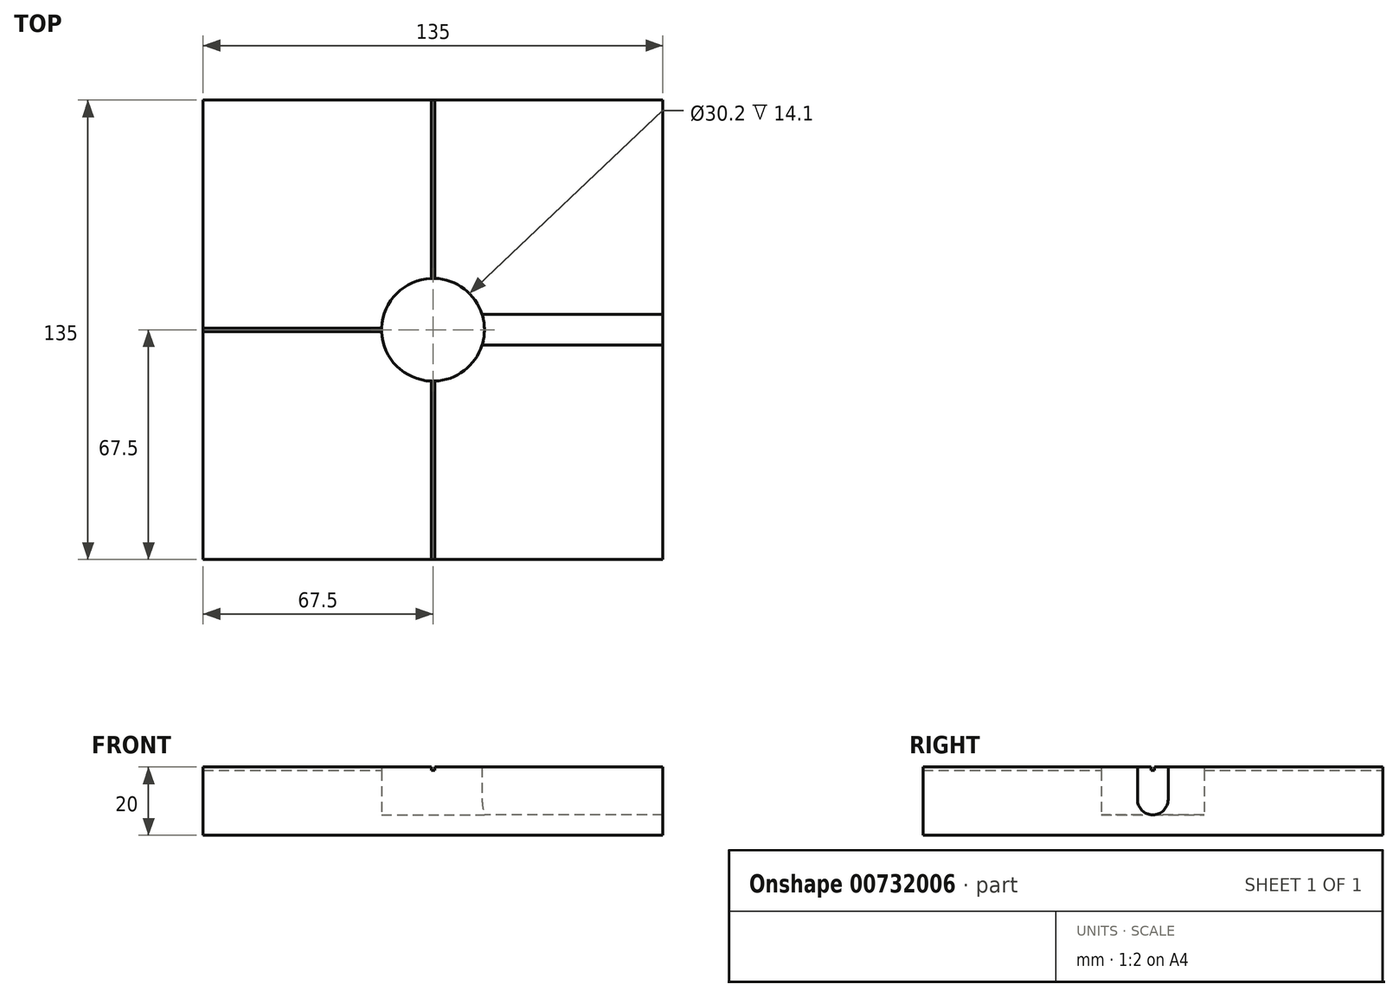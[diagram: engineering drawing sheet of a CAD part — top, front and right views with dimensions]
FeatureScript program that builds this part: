
annotation { "Feature Type Name" : "Feature", "Feature Type Description" : "" }
export const myFeature = defineFeature(function(context is Context, id is Id, definition is map)
    precondition{}
    {
        {
            var Q0;
            Q0=qCreatedBy(makeId("Front.planeOp"),FACE);
            var sketch = newSketch(context, id + "F0", { "sketchPlane" : qUnion([Q0])});
            skLineSegment(sketch, "E0", {"start": v(15.1, 20) * mm, "end": v(15.1, 5.9) * mm});
            skLineSegment(sketch, "E1", {"start": v(15.1, 5.9) * mm, "end": v(0, 5.9) * mm});
            skLineSegment(sketch, "E2", {"start": v(15.1, 20) * mm, "end": v(0, 20) * mm});
            skLineSegment(sketch, "E3", {"start": v(0, 20) * mm, "end": v(0, 5.9) * mm});
            skSolve(sketch);
        }
        {
            var Q0;
            Q0=qCreatedBy(makeId("Right.planeOp"),FACE);
            var sketch = newSketch(context, id + "F1", { "sketchPlane" : qUnion([Q0])});
            skLineSegment(sketch, "E4", {"start": v(0, 20.46) * mm, "end": v(-4.5, 20.46) * mm});
            skLineSegment(sketch, "E5", {"start": v(4.5, 20.46) * mm, "end": v(0, 20.46) * mm});
            skLineSegment(sketch, "E6", {"start": v(4.5, 20.46) * mm, "end": v(4.5, 10.46) * mm});
            skLineSegment(sketch, "E7", {"start": v(-4.5, 20.46) * mm, "end": v(-4.5, 10.46) * mm});
            skArc(sketch, "E8", {"start": v(4.5, 10.46) * mm, "mid": v(0, 5.96) * mm, "end": v(-4.5, 10.46) * mm});
            skSolve(sketch);
        }
        {
            var Q0;
            Q0=qCreatedBy(makeId("Top.planeOp"),FACE);
            var sketch = newSketch(context, id + "F2", { "sketchPlane" : qUnion([Q0])});
            skLineSegment(sketch, "E9", {"start": v(14, 0) * mm, "end": v(14, -0.5) * mm});
            skLineSegment(sketch, "E10", {"start": v(14, 0) * mm, "end": v(14, 0.5) * mm});
            skLineSegment(sketch, "E11", {"start": v(14, 0.5) * mm, "end": v(74, 0.5) * mm});
            skLineSegment(sketch, "E12", {"start": v(74, 0.5) * mm, "end": v(74, -0.5) * mm});
            skLineSegment(sketch, "E13", {"start": v(74, -0.5) * mm, "end": v(14, -0.5) * mm});
            skLineSegment(sketch, "E14", {"start": v(0, -14) * mm, "end": v(-0.5, -14) * mm});
            skLineSegment(sketch, "E15", {"start": v(0, -14) * mm, "end": v(0.5, -14) * mm});
            skLineSegment(sketch, "E16", {"start": v(0.5, -14) * mm, "end": v(0.5, -74) * mm});
            skLineSegment(sketch, "E17", {"start": v(0.5, -74) * mm, "end": v(-0.5, -74) * mm});
            skLineSegment(sketch, "E18", {"start": v(-0.5, -74) * mm, "end": v(-0.5, -14) * mm});
            skLineSegment(sketch, "E19", {"start": v(-14, 0) * mm, "end": v(-14, 0.5) * mm});
            skLineSegment(sketch, "E20", {"start": v(-14, 0) * mm, "end": v(-14, -0.5) * mm});
            skLineSegment(sketch, "E21", {"start": v(-14, -0.5) * mm, "end": v(-74, -0.5) * mm});
            skLineSegment(sketch, "E22", {"start": v(-74, -0.5) * mm, "end": v(-74, 0.5) * mm});
            skLineSegment(sketch, "E23", {"start": v(-74, 0.5) * mm, "end": v(-14, 0.5) * mm});
            skLineSegment(sketch, "E24", {"start": v(-0.5, 14) * mm, "end": v(-0.5, 74) * mm});
            skLineSegment(sketch, "E25", {"start": v(0.5, 74) * mm, "end": v(0.5, 14) * mm});
            skLineSegment(sketch, "E26", {"start": v(-0.5, 14) * mm, "end": v(0, 14) * mm});
            skLineSegment(sketch, "E27", {"start": v(0, 14) * mm, "end": v(0.5, 14) * mm});
            skLineSegment(sketch, "E28", {"start": v(-0.5, 74) * mm, "end": v(0.5, 74) * mm});
            skSolve(sketch);
        }
        {
            var Q0;
            Q0=qCreatedBy(makeId("Top.planeOp"),FACE);
            var sketch = newSketch(context, id + "F3", { "sketchPlane" : qUnion([Q0])});
            skLineSegment(sketch, "E29.bottom", {"start": v(-67.5, 67.5) * mm, "end": v(67.5, 67.5) * mm});
            skLineSegment(sketch, "E29.top", {"start": v(-67.5, -67.5) * mm, "end": v(67.5, -67.5) * mm});
            skLineSegment(sketch, "E29.left", {"start": v(-67.5, 67.5) * mm, "end": v(-67.5, -67.5) * mm});
            skLineSegment(sketch, "E29.right", {"start": v(67.5, 67.5) * mm, "end": v(67.5, -67.5) * mm});
            skSolve(sketch);
        }
        {
            var Q0;
            Q0=makeQuery(id+"F3.imprint","IMPRINT",FACE,{"disambiguationData":[TD([[makeQuery(id+"F3.imprint","IMPRINT",EDGE,{"derivedFrom":sQuery(id+"F3.wireOp",EDGE,"E29.bottom")}),-1.0]])]});
            extrude(context, id + "F4", {"entities" : qUnion([Q0]), "depth" : 20 * mm, "offsetDistance" : 25 * mm});
        }
        {
            var Q0;
            Q0=makeQuery(id+"F0.imprint","IMPRINT",FACE,{"disambiguationData":[TD([[makeQuery(id+"F0.imprint","IMPRINT",EDGE,{"derivedFrom":sQuery(id+"F0.wireOp",EDGE,"E0")}),-1.0]])]});
            var Q1;
            Q1=sQuery(id+"F0.wireOp",EDGE,"E3");
            revolve(context, id + "F5", {"operationType" : NewBodyOperationType.REMOVE, "surfaceOperationType" : NewSurfaceOperationType.NEW, "entities" : qUnion([Q0]), "axis" : qUnion([Q1]), "revolveType" : RevolveType.FULL, "oppositeDirection" : true});
        }
        {
            var Q0;
            Q0=makeQuery(id+"F1.imprint","IMPRINT",FACE,{"disambiguationData":[TD([[makeQuery(id+"F1.imprint","IMPRINT",EDGE,{"derivedFrom":sQuery(id+"F1.wireOp",EDGE,"E4")}),1.0]])]});
            extrude(context, id + "F6", {"entities" : qUnion([Q0]), "operationType" : NewBodyOperationType.REMOVE, "depth" : 150 * mm, "offsetDistance" : 25 * mm, "hasSecondDirection" : true, "secondDirectionOppositeDirection" : true, "secondDirectionDepth" : -14 * mm});
        }
        {
            var Q0;
            Q0=qSketchRegion(id+"F2",true);
            extrude(context, id + "F7", {"entities" : qUnion([Q0]), "operationType" : NewBodyOperationType.REMOVE, "oppositeDirection" : true, "depth" : -25 * mm, "offsetDistance" : 25 * mm, "hasSecondDirection" : true, "secondDirectionOppositeDirection" : true, "secondDirectionDepth" : -19 * mm});
        }
    });
